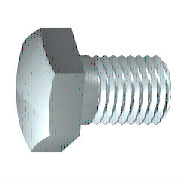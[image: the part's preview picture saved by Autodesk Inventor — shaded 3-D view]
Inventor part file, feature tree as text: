
AUTODESK INVENTOR PART (.ipt)
format: ipt  version: 2023.1 (Build 271208000, 208)  size: 192,000 bytes
history: native  units: mm (DEFAULTED — no unit token found)
features: sketch x3, extrude x1, chamfer x1, plane x1
ambient origin geometry x7: Origin, YZ Plane, XZ Plane, X Axis, Y Axis, Z Axis, Center Point
bodies: Solid1 (feature_tree), Body (feature_tree)
feature tree (6):
  extrude  "Head"  Depth=38.0mm
  chamfer  "Chamfer1"  Distance=9.2mm
  plane  "Work Plane1"
  sketch  "Sketch1"  dims[d0=100.0mm d1=38.0mm]
  sketch  "Sketch2"  dims[d2=16.0mm]
  sketch  "Sketch4"  dims[d12=90.0deg d3=9.2mm d4=0.0mm d5=30.0deg d21=90.0deg d6=0.920175mm d7=0.920275mm d8=0.0mm d9=0.8001mm d10=22.49mm d11=24.0mm d13=0.920275mm d14=16.0mm d15=38.0mm d16=0.0mm d19=24.0mm d55=45.0deg d57=0.0mm d58=0.0mm]
